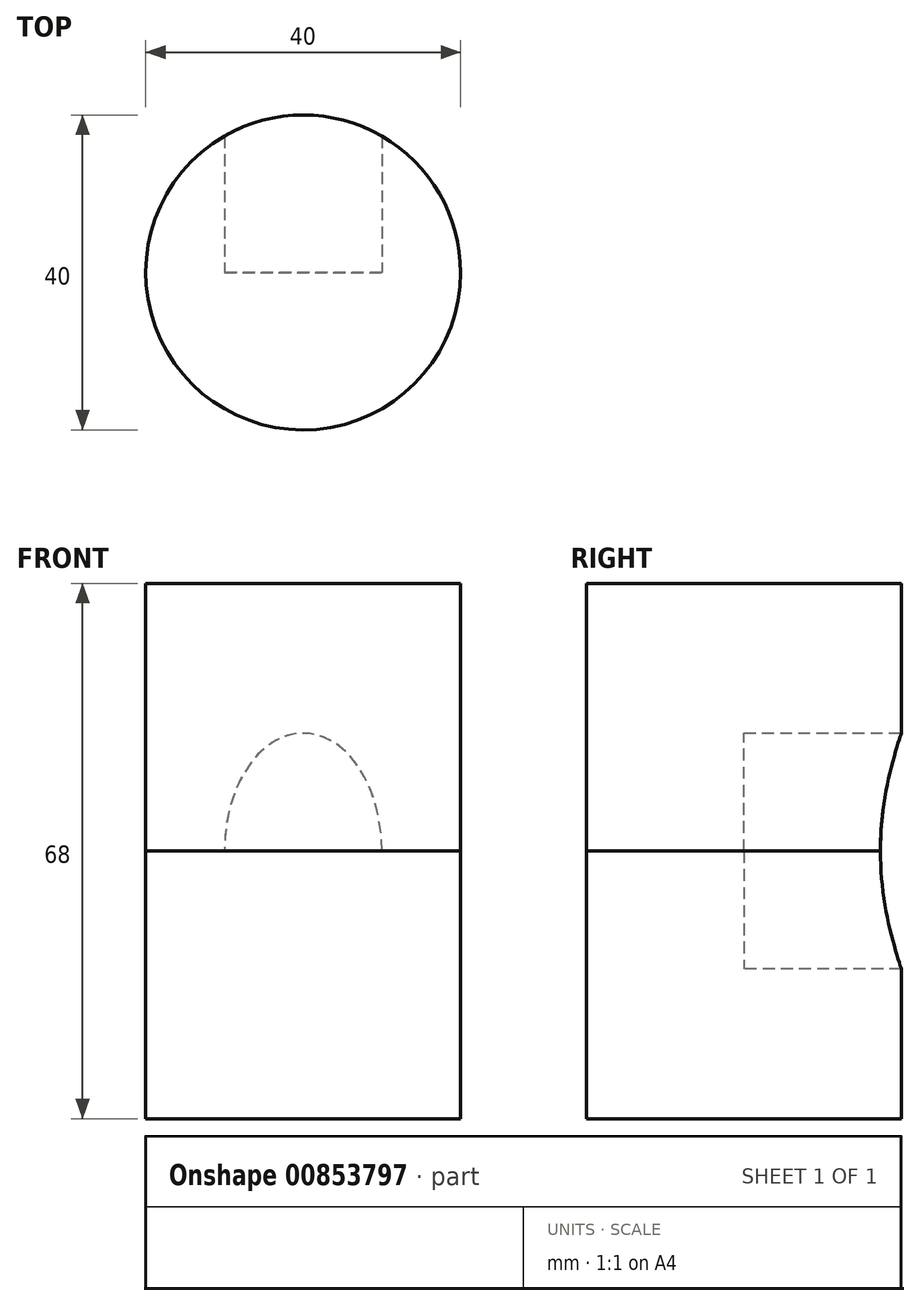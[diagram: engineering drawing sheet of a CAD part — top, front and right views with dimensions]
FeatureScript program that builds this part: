
annotation { "Feature Type Name" : "Feature", "Feature Type Description" : "" }
export const myFeature = defineFeature(function(context is Context, id is Id, definition is map)
    precondition{}
    {
        {
            var Q0;
            Q0=qCreatedBy(makeId("Top.planeOp"),FACE);
            var sketch = newSketch(context, id + "F0", { "sketchPlane" : qUnion([Q0])});
            skCircle(sketch, "E0", {"center": v(0, 0) * mm, "radius": 20 * mm});
            skSolve(sketch);
        }
        {
            var Q0;
            Q0=makeQuery(id+"F0.imprint","IMPRINT",FACE,{"disambiguationData":[TD([[makeQuery(id+"F0.imprint","IMPRINT",EDGE,{"derivedFrom":sQuery(id+"F0.wireOp",EDGE,"E0")}),1.0]])]});
            extrude(context, id + "F1", {"entities" : qUnion([Q0]), "oppositeDirection" : true, "depth" : 34 * mm, "offsetDistance" : 25 * mm});
        }
        {
            var Q0;
            Q0=makeQuery(id+"F1.opExtrude","CAP_FACE",FACE,{"disambiguationData":[OSD([sQuery(id+"F0.wireOp",EDGE,"E0")])],"isStart":true});
            extrude(context, id + "F2", {"entities" : qUnion([Q0]), "depth" : 34 * mm, "offsetDistance" : 25 * mm});
        }
        {
            var Q0;
            Q0=qCreatedBy(makeId("Front.planeOp"),FACE);
            var sketch = newSketch(context, id + "F3", { "sketchPlane" : qUnion([Q0])});
            skEllipse(sketch, "E1", {"center": v(0, 0) * mm, "majorRadius": 15 * mm, "minorRadius": 10 * mm, "majorAxis": v(0, 1)});
            skSolve(sketch);
        }
        {
            var Q0;
            Q0 = qSketchRegion(id + "F3", true);
            extrude(context, id + "F4", {"entities" : qUnion([Q0]), "operationType" : NewBodyOperationType.REMOVE, "oppositeDirection" : true, "depth" : 40 * mm, "offsetDistance" : 25 * mm});
        }
    });
